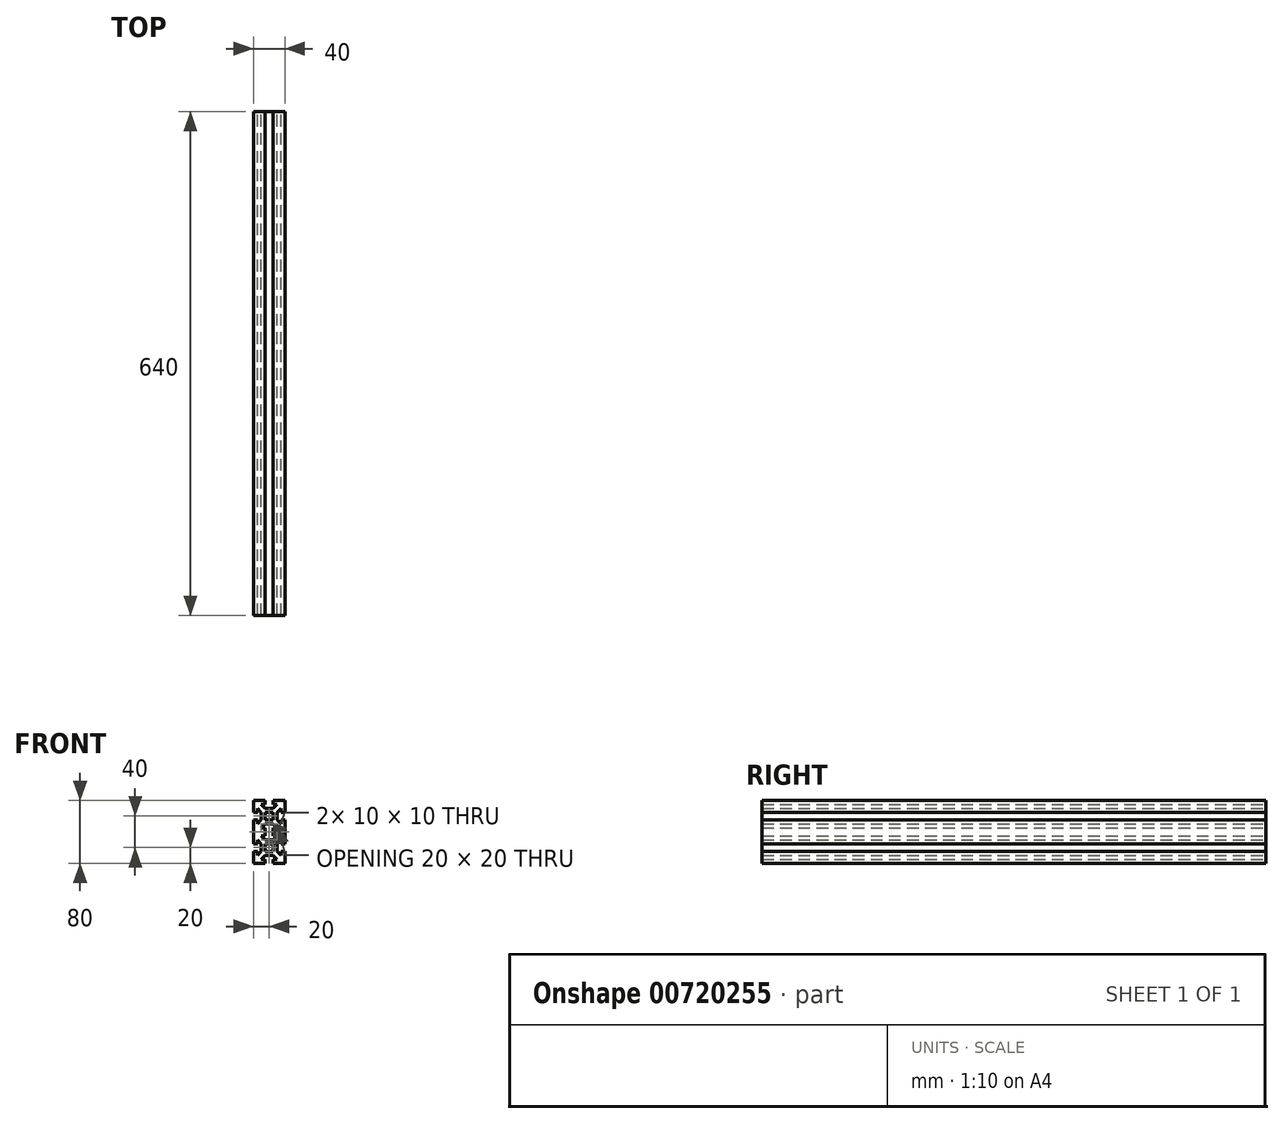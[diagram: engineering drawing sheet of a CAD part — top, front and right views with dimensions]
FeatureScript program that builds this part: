
annotation { "Feature Type Name" : "Feature", "Feature Type Description" : "" }
export const myFeature = defineFeature(function(context is Context, id is Id, definition is map)
    precondition{}
    {
        {
            var Q0;
            Q0=qCreatedBy(makeId("Front.planeOp"),FACE);
            var sketch = newSketch(context, id + "F0", { "sketchPlane" : qUnion([Q0])});
            skLineSegment(sketch, "E0.top", {"start": v(20, -20) * mm, "end": v(5, -20) * mm});
            skLineSegment(sketch, "E0.left", {"start": v(20, 20) * mm, "end": v(20, 5) * mm});
            skLineSegment(sketch, "E0.right", {"start": v(-20, 20) * mm, "end": v(-20, 5) * mm});
            skPoint(sketch, "E0.middle", {"position": v(0, 0) * mm});
            skLineSegment(sketch, "E1", {"start": v(0, 20) * mm, "end": v(0, -20) * mm, "construction": true});
            skLineSegment(sketch, "E2", {"start": v(-20, 0) * mm, "end": v(20, 0) * mm, "construction": true});
            skLineSegment(sketch, "E3", {"start": v(-20, 5) * mm, "end": v(-15, 5) * mm});
            skLineSegment(sketch, "E4", {"start": v(-20, -5) * mm, "end": v(-15, -5) * mm});
            skLineSegment(sketch, "E5", {"start": v(-5, 20) * mm, "end": v(-5, 15) * mm});
            skLineSegment(sketch, "E6", {"start": v(5, 20) * mm, "end": v(5, 15) * mm});
            skLineSegment(sketch, "E7", {"start": v(-10, 15) * mm, "end": v(-5, 15) * mm});
            skLineSegment(sketch, "E8", {"start": v(-10, -15) * mm, "end": v(-5, -15) * mm});
            skLineSegment(sketch, "E9", {"start": v(15, 10) * mm, "end": v(15, 5) * mm});
            skLineSegment(sketch, "E10", {"start": v(-15, 10) * mm, "end": v(-10, 5) * mm});
            skLineSegment(sketch, "E11", {"start": v(-10, 15) * mm, "end": v(-5, 10) * mm});
            skLineSegment(sketch, "E12", {"start": v(-15, -10) * mm, "end": v(-10, -5) * mm});
            skLineSegment(sketch, "E13", {"start": v(-10, -15) * mm, "end": v(-5, -10) * mm});
            skLineSegment(sketch, "E14.trimOffspring", {"start": v(20, -5) * mm, "end": v(20, -20) * mm});
            skLineSegment(sketch, "E15.trimOffspring", {"start": v(-20, -5) * mm, "end": v(-20, -20) * mm});
            skLineSegment(sketch, "E16.trimOffspring", {"start": v(-5, -20) * mm, "end": v(-20, -20) * mm});
            skLineSegment(sketch, "E17.trimOffspring", {"start": v(5, 15) * mm, "end": v(10, 15) * mm});
            skLineSegment(sketch, "E18.trimOffspring", {"start": v(-15, -5) * mm, "end": v(-15, -10) * mm});
            skLineSegment(sketch, "E19.trimOffspring", {"start": v(15, -5) * mm, "end": v(15, -10) * mm});
            skLineSegment(sketch, "E20.trimOffspring", {"start": v(5, -15) * mm, "end": v(10, -15) * mm});
            skLineSegment(sketch, "E21.trimOffspring", {"start": v(-5, 5) * mm, "end": v(-5, -5) * mm});
            skLineSegment(sketch, "E22.trimOffspring", {"start": v(5, 5) * mm, "end": v(5, -5) * mm});
            skLineSegment(sketch, "E23.trimOffspring", {"start": v(15, 5) * mm, "end": v(20, 5) * mm});
            skLineSegment(sketch, "E24.trimOffspring", {"start": v(15, -5) * mm, "end": v(20, -5) * mm});
            skLineSegment(sketch, "E25.trimOffspring", {"start": v(5, -15) * mm, "end": v(5, -20) * mm});
            skLineSegment(sketch, "E26.trimOffspring", {"start": v(-5, -15) * mm, "end": v(-5, -20) * mm});
            skLineSegment(sketch, "E27.trimOffspring", {"start": v(-5, -5) * mm, "end": v(5, -5) * mm});
            skLineSegment(sketch, "E28.trimOffspring", {"start": v(-5, 5) * mm, "end": v(5, 5) * mm});
            skLineSegment(sketch, "E29", {"start": v(10, 5) * mm, "end": v(10, -5) * mm});
            skLineSegment(sketch, "E30", {"start": v(-5, 10) * mm, "end": v(5, 10) * mm});
            skLineSegment(sketch, "E31", {"start": v(-10, 5) * mm, "end": v(-10, -5) * mm});
            skLineSegment(sketch, "E32", {"start": v(-5, -10) * mm, "end": v(5, -10) * mm});
            skLineSegment(sketch, "E33.trimOffspring", {"start": v(-15, 10) * mm, "end": v(-15, 5) * mm});
            skPoint(sketch, "E34.orphan", {"position": v(20, 15) * mm});
            skPoint(sketch, "E35.orphan", {"position": v(20, -15) * mm});
            skPoint(sketch, "E36.orphan", {"position": v(15, -20) * mm});
            skPoint(sketch, "E37.orphan", {"position": v(-15, -20) * mm});
            skLineSegment(sketch, "E38.trimOffspring", {"start": v(-5, 0) * mm, "end": v(0, -5) * mm});
            skLineSegment(sketch, "E39.trimOffspring", {"start": v(-5, 0) * mm, "end": v(0, 5) * mm});
            skLineSegment(sketch, "E40.trimOffspring", {"start": v(0, 5) * mm, "end": v(5, 0) * mm});
            skLineSegment(sketch, "E41.trimOffspring", {"start": v(5, 10) * mm, "end": v(10, 15) * mm});
            skLineSegment(sketch, "E42.trimOffspring", {"start": v(10, 5) * mm, "end": v(15, 10) * mm});
            skLineSegment(sketch, "E43.trimOffspring", {"start": v(10, -5) * mm, "end": v(15, -10) * mm});
            skLineSegment(sketch, "E44.trimOffspring", {"start": v(5, -10) * mm, "end": v(10, -15) * mm});
            skLineSegment(sketch, "E45.trimOffspring", {"start": v(0, -5) * mm, "end": v(5, 0) * mm});
            skLineSegment(sketch, "E46.bottom", {"start": v(20, 60) * mm, "end": v(5, 60) * mm});
            skLineSegment(sketch, "E46.left", {"start": v(20, 60) * mm, "end": v(20, 45) * mm});
            skLineSegment(sketch, "E46.right", {"start": v(-20, 60) * mm, "end": v(-20, 45) * mm});
            skPoint(sketch, "E46.middle", {"position": v(0, 40) * mm});
            skLineSegment(sketch, "E47", {"start": v(0, 60) * mm, "end": v(0, 20) * mm, "construction": true});
            skLineSegment(sketch, "E48", {"start": v(-20, 40) * mm, "end": v(20, 40) * mm, "construction": true});
            skLineSegment(sketch, "E49", {"start": v(-20, 45) * mm, "end": v(-15, 45) * mm});
            skLineSegment(sketch, "E50", {"start": v(-20, 35) * mm, "end": v(-15, 35) * mm});
            skLineSegment(sketch, "E51", {"start": v(-5, 60) * mm, "end": v(-5, 55) * mm});
            skLineSegment(sketch, "E52", {"start": v(5, 60) * mm, "end": v(5, 55) * mm});
            skLineSegment(sketch, "E53", {"start": v(-10, 55) * mm, "end": v(-5, 55) * mm});
            skLineSegment(sketch, "E54", {"start": v(-10, 25) * mm, "end": v(-5, 25) * mm});
            skLineSegment(sketch, "E55", {"start": v(15, 50) * mm, "end": v(15, 45) * mm});
            skLineSegment(sketch, "E56", {"start": v(-15, 50) * mm, "end": v(-10, 45) * mm});
            skLineSegment(sketch, "E57", {"start": v(-10, 55) * mm, "end": v(-5, 50) * mm});
            skLineSegment(sketch, "E58", {"start": v(-15, 30) * mm, "end": v(-10, 35) * mm});
            skLineSegment(sketch, "E59", {"start": v(-10, 25) * mm, "end": v(-5, 30) * mm});
            skLineSegment(sketch, "E60.trimOffspring", {"start": v(20, 35) * mm, "end": v(20, 20) * mm});
            skLineSegment(sketch, "E61.trimOffspring", {"start": v(-20, 35) * mm, "end": v(-20, 20) * mm});
            skLineSegment(sketch, "E62.trimOffspring", {"start": v(-5, 60) * mm, "end": v(-20, 60) * mm});
            skLineSegment(sketch, "E63.trimOffspring", {"start": v(5, 55) * mm, "end": v(10, 55) * mm});
            skLineSegment(sketch, "E64.trimOffspring", {"start": v(-15, 35) * mm, "end": v(-15, 30) * mm});
            skLineSegment(sketch, "E65.trimOffspring", {"start": v(15, 35) * mm, "end": v(15, 30) * mm});
            skLineSegment(sketch, "E66.trimOffspring", {"start": v(5, 25) * mm, "end": v(10, 25) * mm});
            skLineSegment(sketch, "E67.trimOffspring", {"start": v(-5, 45) * mm, "end": v(-5, 35) * mm});
            skLineSegment(sketch, "E68.trimOffspring", {"start": v(5, 45) * mm, "end": v(5, 35) * mm});
            skLineSegment(sketch, "E69.trimOffspring", {"start": v(15, 45) * mm, "end": v(20, 45) * mm});
            skLineSegment(sketch, "E70.trimOffspring", {"start": v(15, 35) * mm, "end": v(20, 35) * mm});
            skLineSegment(sketch, "E71.trimOffspring", {"start": v(5, 25) * mm, "end": v(5, 20) * mm});
            skLineSegment(sketch, "E72.trimOffspring", {"start": v(-5, 25) * mm, "end": v(-5, 20) * mm});
            skLineSegment(sketch, "E73.trimOffspring", {"start": v(-5, 35) * mm, "end": v(5, 35) * mm});
            skLineSegment(sketch, "E74.trimOffspring", {"start": v(-5, 45) * mm, "end": v(5, 45) * mm});
            skLineSegment(sketch, "E75", {"start": v(10, 45) * mm, "end": v(10, 35) * mm});
            skLineSegment(sketch, "E76", {"start": v(-5, 50) * mm, "end": v(5, 50) * mm});
            skLineSegment(sketch, "E77", {"start": v(-10, 45) * mm, "end": v(-10, 35) * mm});
            skLineSegment(sketch, "E78", {"start": v(-5, 30) * mm, "end": v(5, 30) * mm});
            skLineSegment(sketch, "E79.trimOffspring", {"start": v(-15, 50) * mm, "end": v(-15, 45) * mm});
            skPoint(sketch, "E80.orphan", {"position": v(20, 55) * mm});
            skPoint(sketch, "E81.orphan", {"position": v(20, 25) * mm});
            skPoint(sketch, "E82.orphan", {"position": v(15, 20) * mm});
            skLineSegment(sketch, "E83.trimOffspring", {"start": v(-5, 40) * mm, "end": v(0, 35) * mm});
            skLineSegment(sketch, "E84.trimOffspring", {"start": v(-5, 40) * mm, "end": v(0, 45) * mm});
            skLineSegment(sketch, "E85.trimOffspring", {"start": v(0, 45) * mm, "end": v(5, 40) * mm});
            skLineSegment(sketch, "E86.trimOffspring", {"start": v(5, 50) * mm, "end": v(10, 55) * mm});
            skLineSegment(sketch, "E87.trimOffspring", {"start": v(10, 45) * mm, "end": v(15, 50) * mm});
            skLineSegment(sketch, "E88.trimOffspring", {"start": v(10, 35) * mm, "end": v(15, 30) * mm});
            skLineSegment(sketch, "E89.trimOffspring", {"start": v(5, 30) * mm, "end": v(10, 25) * mm});
            skLineSegment(sketch, "E90.trimOffspring", {"start": v(0, 35) * mm, "end": v(5, 40) * mm});
            skSolve(sketch);
        }
        {
            var Q0;
            Q0=makeQuery(id+"F0.imprint","IMPRINT",FACE,{"disambiguationData":[TD([[makeQuery(id+"F0.imprint","IMPRINT",EDGE,{"derivedFrom":sQuery(id+"F0.wireOp",EDGE,"E0.top")}),-1.0]])]});
            extrude(context, id + "F1", {"entities" : qUnion([Q0]), "depth" : 640 * mm, "offsetDistance" : 25 * mm});
        }
    });
